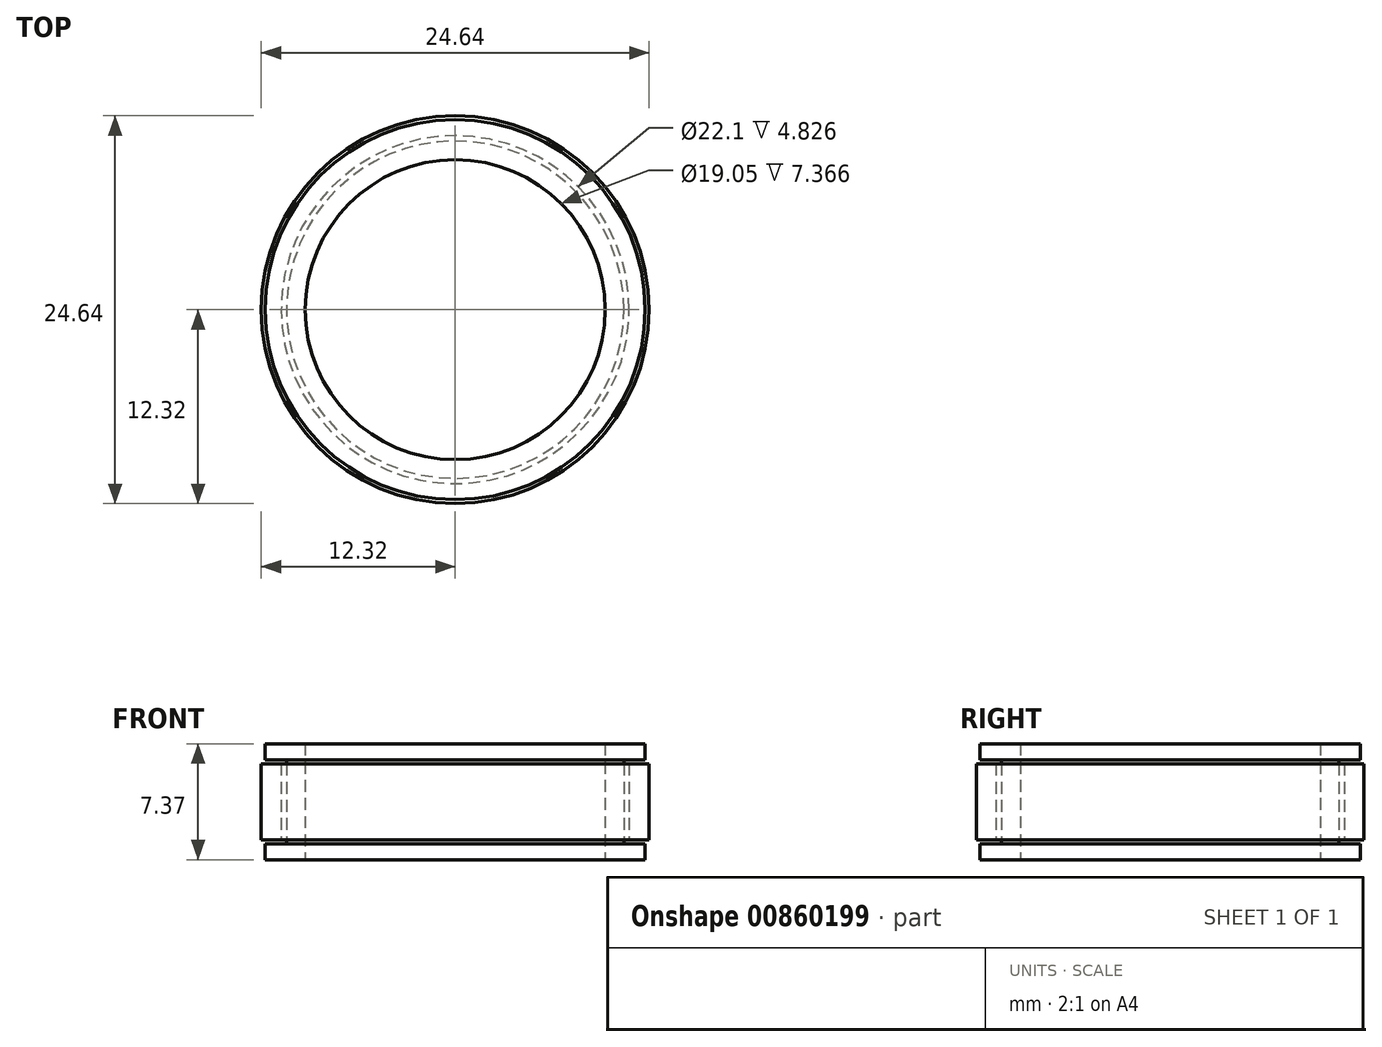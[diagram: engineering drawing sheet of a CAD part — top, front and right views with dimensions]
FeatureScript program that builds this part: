
annotation { "Feature Type Name" : "Feature", "Feature Type Description" : "" }
export const myFeature = defineFeature(function(context is Context, id is Id, definition is map)
    precondition{}
    {
        {
            var Q0;
            Q0=qCreatedBy(makeId("Top.planeOp"),FACE);
            var sketch = newSketch(context, id + "F0", { "sketchPlane" : qUnion([Q0])});
            skCircle(sketch, "E0", {"center": v(0, 0) * mm, "radius": 9.53 * mm});
            skCircle(sketch, "E1", {"center": v(0, 0) * mm, "radius": 12.07 * mm});
            skCircle(sketch, "E2", {"center": v(0, 0) * mm, "radius": 10.72 * mm});
            skSolve(sketch);
        }
        {
            var Q0;
            Q0=makeQuery(id+"F0.imprint","IMPRINT",FACE,{"disambiguationData":[TD([[makeQuery(id+"F0.imprint","IMPRINT",EDGE,{"derivedFrom":sQuery(id+"F0.wireOp",EDGE,"E0")}),-1.0]])]});
            extrude(context, id + "F1", {"entities" : qUnion([Q0]), "depth" : 7.37 * mm, "offsetDistance" : 25.4 * mm});
        }
        {
            var Q0;
            Q0=makeQuery(id+"F0.imprint","IMPRINT",FACE,{"disambiguationData":[TD([[makeQuery(id+"F0.imprint","IMPRINT",EDGE,{"derivedFrom":sQuery(id+"F0.wireOp",EDGE,"E1")}),1.0]])]});
            extrude(context, id + "F2", {"entities" : qUnion([Q0]), "operationType" : NewBodyOperationType.ADD, "depth" : 1.02 * mm, "offsetDistance" : 25.4 * mm});
        }
        {
            var Q0;
            Q0=makeQuery(id+"F0.imprint","IMPRINT",FACE,{"disambiguationData":[TD([[makeQuery(id+"F0.imprint","IMPRINT",EDGE,{"derivedFrom":sQuery(id+"F0.wireOp",EDGE,"E1")}),1.0]])]});
            extrude(context, id + "F3", {"entities" : qUnion([Q0]), "operationType" : NewBodyOperationType.ADD, "depth" : 7.37 * mm, "offsetDistance" : 25.4 * mm, "hasSecondDirection" : true, "secondDirectionOppositeDirection" : false, "secondDirectionDepth" : 6.35 * mm});
        }
        {
            var Q0;
            Q0=makeQuery(id+"F2.opExtrude","CAP_FACE",FACE,{"disambiguationData":[OSD([sQuery(id+"F0.wireOp",EDGE,"E1"),sQuery(id+"F0.wireOp",EDGE,"E2")])],"isStart":false});
            var sketch = newSketch(context, id + "F4", { "sketchPlane" : qUnion([Q0])});
            skCircle(sketch, "E3", {"center": v(0, 0) * mm, "radius": 12.32 * mm});
            skCircle(sketch, "E4", {"center": v(0, 0) * mm, "radius": 11.05 * mm});
            skSolve(sketch);
        }
        {
            var Q0;
            Q0 = qSketchRegion(id + "F4", true);
            extrude(context, id + "F5", {"entities" : qUnion([Q0]), "depth" : 5.08 * mm, "offsetDistance" : 25.4 * mm, "hasSecondDirection" : true, "secondDirectionOppositeDirection" : true, "secondDirectionDepth" : -0.25 * mm});
        }
    });
